FREECAD ASSEMBLY — COMPONENT RECIPES ("m1")

This assembly document has 2 components, labeled P0..P1 below (a component is one placed body or linked part). 0 of them carry a construction recipe — the FreeCAD feature program that regenerates the part from scratch, quoted from this document or its linked companion documents; the rest are supplied as boundary geometry only. No exploded tour is included for this assembly.
COMPONENT P0 — geometry summary ("Body"; no construction recipe available for this part):
  bounding box: 60.0 x 40.0 x 40.0 mm
  tessellated surface: 1,004 triangles
  volume: 75275 mm^3 (78% of its bounding box)
  symmetry: 2-fold rotationally symmetric about the x axis; 2-fold rotationally symmetric about the y axis; revolution-symmetric about the z axis through its bounding-box center; mirror-symmetric across its x mid-plane, z mid-plane
COMPONENT P1 — geometry summary ("Corpo"; no construction recipe available for this part):
  bounding box: 75.0 x 75.0 x 60.0 mm
  tessellated surface: 516 triangles
  volume: 91593 mm^3 (27% of its bounding box)
  symmetry: 4-fold rotationally symmetric about the z axis; mirror-symmetric across its y mid-plane
PROVENANCE & LICENSES
A FreeCAD (.FCStd) document from a public repository crawl; recipes are the document's own serialized feature recipes (and, for linked parts, companion documents' recipes).
License: as declared in the source repository (recorded in the dataset sidecar).
